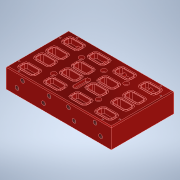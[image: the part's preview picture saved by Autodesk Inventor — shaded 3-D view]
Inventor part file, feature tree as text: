
AUTODESK INVENTOR PART (.ipt)
format: ipt  version: 2022 (Build 260153000, 153)  size: 869,376 bytes
history: native  units: mm
features: extrude x6, hole x6, other x5, sketch x5, chamfer x1
ambient origin geometry x8: Origin, YZ Plane, XZ Plane, XY Plane, X Axis, Y Axis, Z Axis, Center Point
bodies: Volumenkörper1 (feature_tree)
feature tree (23):
  other  "Annotations"
  extrude  "Extrusion1"  Depth=44.45mm
  chamfer  "Fase1"  Distance=44.45mm
  other  "Alignment Holes"
  hole  "Bohrung7"  [1 undecoded]
  other  "Wells"
  extrude  "Extrusion6"  Depth=5.0mm
  extrude  "Extrusion7"  Depth=24.0mm
  sketch  "Sketch17"  dims[d11=2.0mm d12=2.0mm d13=45.0deg d153=24.0mm]
  hole  "Hole12"  [1 undecoded]
  hole  "Hole13"  [1 undecoded]
  sketch  "Sketch19"  dims[d154=24.0mm d155=5.0mm]
  hole  "Hole15"  [1 undecoded]
  hole  "Hole16"  [1 undecoded]
  hole  "Hole18"  [1 undecoded]
  extrude  "Extrusion9"  Depth=6.35mm
  sketch  "Sketch24"  dims[d158=5.0mm d159=5.0mm d160=24.0mm d161=24.0mm d162=5.0mm d163=5.0mm d164=24.0mm d165=5.0mm d166=24.0mm d167=5.0mm d168=24.0mm d169=3.242mm d170=6.0mm d171=8.0mm d172=4.6mm d173=14.3117mm d174=20.0mm d175=20.594885mm d259=30.0mm d260=15.0mm d261=8.5mm d262=11.5mm d266=3.0mm d267=40.0mm d269=57.317mm d270=20.0mm d272=35.566mm d276=11.499mm d277=10.0mm d278=0.0mm d279=30.0mm d280=0.0mm d283=10.0mm d284=20.0mm d286=59.317mm d287=10.0mm d289=10.0mm d291=7.9502mm d292=6.92404mm d293=0.624793mm d294=8.304022mm d295=4.0mm d296=2.0mm d297=90.0deg d298=20.0mm d299=20.594885mm d300=7.9502mm d301=6.92404mm d302=0.624793mm d303=8.304022mm d304=4.0mm d305=2.0mm d306=90.0deg d307=55.0mm d308=20.594885mm d326=20.0mm d328=59.317mm d329=10.0mm d331=10.0mm d333=7.9502mm d334=6.92404mm d335=0.624793mm d336=8.304022mm d337=4.0mm d338=2.0mm d339=90.0deg d340=55.0mm d341=20.594885mm d342=7.9502mm d343=6.92404mm d344=0.624793mm d345=8.304022mm d346=4.0mm d347=2.0mm d348=90.0deg d349=20.0mm d350=20.594885mm d382=50.0mm d383=100.0mm d384=31.0mm d385=62.0mm d386=6.5278mm d387=6.0mm d388=11.1252mm d389=6.35mm d390=14.3117mm d391=8.0mm d392=20.594885mm d410=11.5mm d411=8.5mm d412=15.0mm d413=30.0mm d414=3.0mm d415=40.0mm d417=57.317mm d418=20.0mm d420=35.566mm d441=2.4892mm d442=0.0mm d443=10.0mm d444=10.0mm d446=12.5mm d447=12.5mm d448=12.5mm d449=12.5mm d450=20.0mm d451=12.5mm d452=12.5mm d453=1.27mm d454=1.27mm d456=1.27mm d457=1.27mm d458=3.175mm d459=3.175mm d460=3.175mm d461=3.175mm d462=40.0mm d464=57.3278mm d465=20.0mm d467=35.56mm d470=25.4mm d471=0.0mm d472=0.0mm d473=6.35mm d474=0.0mm]
  extrude  "Extrusion10"  Depth=6.35mm
  extrude  "Extrusion11"  Depth=6.35mm
  sketch  "Skizze1"  dims[d0=234.95mm d2=139.7mm d3=44.45mm d4=0.0mm]
  sketch  "Sketch22"  dims[d156=5.0mm d157=24.0mm]
  other  "Seal Seating"
  other  "General Note 1"
note: 6 required parameter values undecoded (feature->parameter linkage not recoverable at this tier; creation-order binding heuristic only, values carry confidence <= 0.55)
